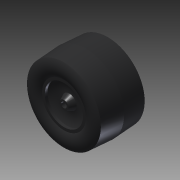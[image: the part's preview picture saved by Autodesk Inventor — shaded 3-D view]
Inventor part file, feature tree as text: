
AUTODESK INVENTOR PART (.ipt)
format: ipt  version: 2013 (Build 170138000, 138)  size: 151,040 bytes
history: native  units: in
note: dims shown in document units (in); Inventor stores cm internally (conversion verified against a paired STEP export)
features: revolve x1, sketch x1
ambient origin geometry x8: Origin, YZ Plane, XZ Plane, XY Plane, X Axis, Y Axis, Z Axis, Center Point
bodies: Solid1 (feature_tree)
feature tree (2):
  revolve  "Revolution1"  [1 undecoded]
  sketch  "Sketch1"  dims[d0=0.0625in d1=0.0394in d2=0.125in d3=0.0625in d4=0.4375in d5=0.5in d6=0.0625in d7=0.8438in d8=0.875in d9=0.5in d10=0.5in d11=0.0in d13=0.5in d14=0.8438in d15=0.125in d16=0.75in d17=0.0938in d18=0.25in d19=0.25in d20=0.5in d21=0.3769in d22=0.2753in d23=90.0deg]
note: 1 required parameter value undecoded (feature->parameter linkage not recoverable at this tier; creation-order binding heuristic only, values carry confidence <= 0.55)
